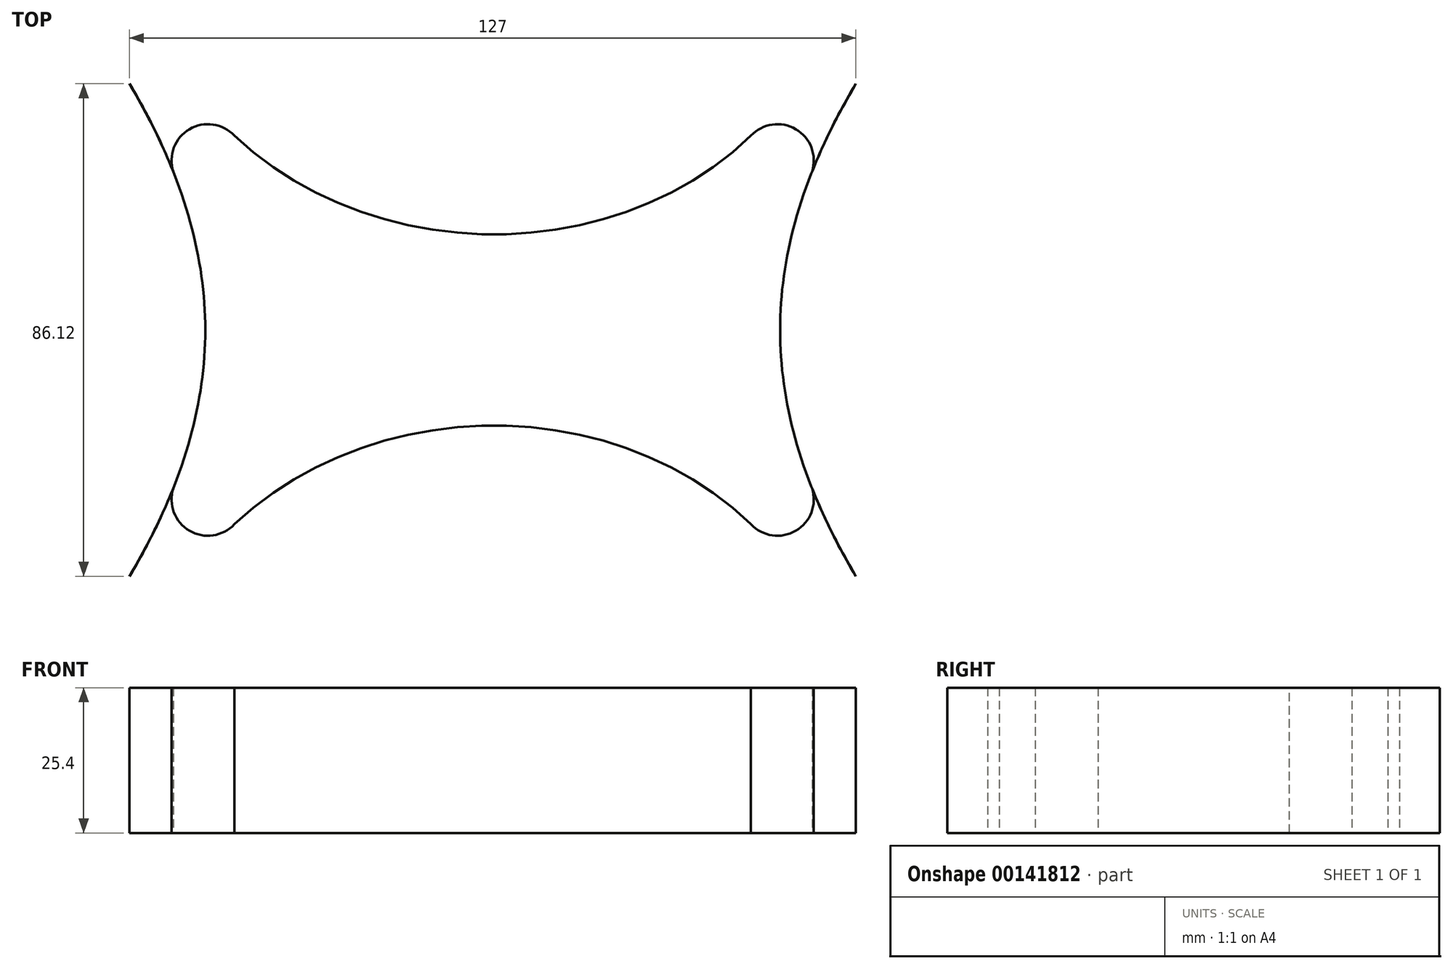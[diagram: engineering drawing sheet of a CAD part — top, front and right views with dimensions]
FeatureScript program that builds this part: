
annotation { "Feature Type Name" : "Feature", "Feature Type Description" : "" }
export const myFeature = defineFeature(function(context is Context, id is Id, definition is map)
    precondition{}
    {
        {
            var Q0;
            Q0=qCreatedBy(makeId("Top.planeOp"),FACE);
            var sketch = newSketch(context, id + "F0", { "sketchPlane" : qUnion([Q0])});
            skFitSpline(sketch, "E0", {"points": [v(-38.1, 43.06) * mm, v(-38.1, -43.06) * mm], "startDerivative": vector(53.34, -90.05) * mm, "endDerivative": vector(-52.65, -88.67) * mm});
            skArc(sketch, "E1.filletArc", {"start": v(-19.76, 33.98) * mm, "mid": v(-27.79, 35) * mm, "end": v(-30.3, 27.31) * mm});
            skFitSpline(sketch, "E2.MirrorCS", {"points": [v(-38.1, -43.06) * mm, v(-38.1, 43.06) * mm], "startDerivative": vector(53.34, 90.05) * mm, "endDerivative": vector(-52.65, 88.67) * mm});
            skArc(sketch, "E3.MirrorCS", {"start": v(-19.76, -33.98) * mm, "mid": v(-27.79, -35) * mm, "end": v(-30.3, -27.31) * mm});
            skFitSpline(sketch, "E4.MirrorCS", {"points": [v(88.9, 43.06) * mm, v(88.9, -43.06) * mm], "startDerivative": vector(-53.34, -90.05) * mm, "endDerivative": vector(52.65, -88.67) * mm});
            skArc(sketch, "E5.MirrorCS", {"start": v(70.56, 33.98) * mm, "mid": v(78.59, 35) * mm, "end": v(81.1, 27.31) * mm});
            skFitSpline(sketch, "E6.MirrorCS", {"points": [v(88.9, -43.06) * mm, v(88.9, 43.06) * mm], "startDerivative": vector(-53.34, 90.05) * mm, "endDerivative": vector(52.65, 88.67) * mm});
            skArc(sketch, "E7.MirrorCS", {"start": v(70.56, -33.98) * mm, "mid": v(78.59, -35) * mm, "end": v(81.1, -27.31) * mm});
            skFitSpline(sketch, "E8", {"points": [v(-19.76, -33.98) * mm, v(70.56, -33.98) * mm], "startDerivative": vector(73.84, 69.02) * mm, "endDerivative": vector(71.76, -69.02) * mm});
            skFitSpline(sketch, "E9.MirrorCS", {"points": [v(-19.76, 33.98) * mm, v(70.56, 33.98) * mm], "startDerivative": vector(73.84, -69.02) * mm, "endDerivative": vector(71.76, 69.02) * mm});
            skSolve(sketch);
        }
        {
            var Q0;
            Q0 = qSketchRegion(id + "F0", true);
            extrude(context, id + "F1", {"entities" : qUnion([Q0]), "depth" : 25.4 * mm});
        }
    });
